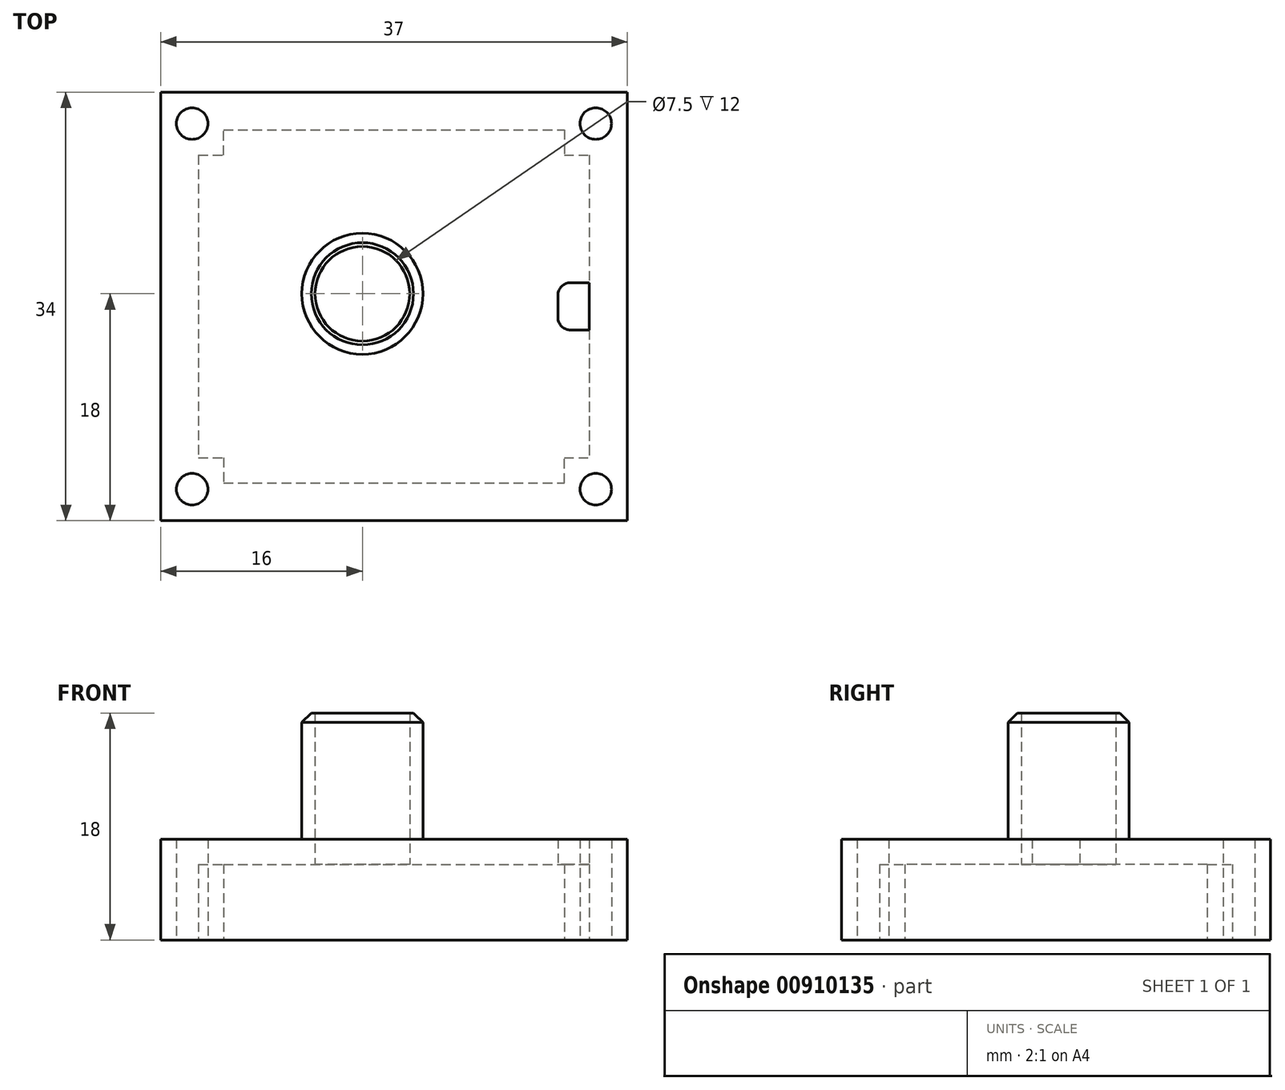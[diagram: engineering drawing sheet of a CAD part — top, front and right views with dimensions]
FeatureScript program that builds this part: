
annotation { "Feature Type Name" : "Feature", "Feature Type Description" : "" }
export const myFeature = defineFeature(function(context is Context, id is Id, definition is map)
    precondition{}
    {
        {
            var Q0;
            Q0=qCreatedBy(makeId("Top.planeOp"),FACE);
            var sketch = newSketch(context, id + "F0", { "sketchPlane" : qUnion([Q0])});
            skCircle(sketch, "E0", {"center": v(0, 0) * mm, "radius": 3.75 * mm});
            skCircle(sketch, "E1", {"center": v(0, 0) * mm, "radius": 4.8 * mm});
            skLineSegment(sketch, "E2.bottom", {"start": v(-13, 13) * mm, "end": v(18, 13) * mm});
            skLineSegment(sketch, "E2.top", {"start": v(-13, -15) * mm, "end": v(18, -15) * mm});
            skLineSegment(sketch, "E2.left", {"start": v(-13, 13) * mm, "end": v(-13, -15) * mm});
            skLineSegment(sketch, "E2.right", {"start": v(18, 13) * mm, "end": v(18, -15) * mm});
            skLineSegment(sketch, "E3.bottom", {"start": v(-16, 16) * mm, "end": v(21, 16) * mm});
            skLineSegment(sketch, "E3.top", {"start": v(-16, -18) * mm, "end": v(21, -18) * mm});
            skLineSegment(sketch, "E3.left", {"start": v(-16, 16) * mm, "end": v(-16, -18) * mm});
            skLineSegment(sketch, "E3.right", {"start": v(21, 16) * mm, "end": v(21, -18) * mm});
            skCircle(sketch, "E4", {"center": v(-13.5, 13.5) * mm, "radius": 1.25 * mm});
            skCircle(sketch, "E5", {"center": v(18.5, 13.5) * mm, "radius": 1.25 * mm});
            skCircle(sketch, "E6", {"center": v(18.5, -15.5) * mm, "radius": 1.25 * mm});
            skCircle(sketch, "E7", {"center": v(-13.5, -15.5) * mm, "radius": 1.25 * mm});
            skLineSegment(sketch, "E8.bottom", {"start": v(18, 0.88) * mm, "end": v(15.5, 0.88) * mm});
            skLineSegment(sketch, "E8.top", {"start": v(18, -2.87) * mm, "end": v(15.5, -2.87) * mm});
            skLineSegment(sketch, "E8.left", {"start": v(18, 0.88) * mm, "end": v(18, -2.87) * mm});
            skLineSegment(sketch, "E8.right", {"start": v(15.5, 0.88) * mm, "end": v(15.5, -2.87) * mm});
            skLineSegment(sketch, "E9", {"start": v(-13, -13) * mm, "end": v(-11, -13) * mm});
            skLineSegment(sketch, "E10", {"start": v(-11, -13) * mm, "end": v(-11, -15) * mm});
            skLineSegment(sketch, "E11", {"start": v(16, -15) * mm, "end": v(16, -13) * mm});
            skLineSegment(sketch, "E12", {"start": v(16, -13) * mm, "end": v(18, -13) * mm});
            skLineSegment(sketch, "E13", {"start": v(-13, 11) * mm, "end": v(-11, 11) * mm});
            skLineSegment(sketch, "E14", {"start": v(-11, 11) * mm, "end": v(-11, 13) * mm});
            skLineSegment(sketch, "E15", {"start": v(16, 13) * mm, "end": v(16, 11) * mm});
            skLineSegment(sketch, "E16", {"start": v(16, 11) * mm, "end": v(18, 11) * mm});
            skSolve(sketch);
        }
        {
            var Q0;
            {var subQ3=sQuery(id+"F0.wireOp",EDGE,"E2.bottom");Q0=makeQuery(id+"F0.imprint","IMPRINT",FACE,{"disambiguationData":[TD([[makeQuery(id+"F0.imprint","IMPRINT",EDGE,{"derivedFrom":subQ3}),1.0]])]});}
            var Q1;
            {var subQ4=sQuery(id+"F0.wireOp",EDGE,"E9");Q1=makeQuery(id+"F0.imprint","IMPRINT",FACE,{"disambiguationData":[TD([[makeQuery(id+"F0.imprint","IMPRINT",EDGE,{"derivedFrom":subQ4}),-1.0]])]});}
            var Q2;
            {var subQ3=sQuery(id+"F0.wireOp",EDGE,"E11");Q2=makeQuery(id+"F0.imprint","IMPRINT",FACE,{"disambiguationData":[TD([[makeQuery(id+"F0.imprint","IMPRINT",EDGE,{"derivedFrom":subQ3}),-1.0]])]});}
            var Q3;
            {var subQ3=sQuery(id+"F0.wireOp",EDGE,"E15");Q3=makeQuery(id+"F0.imprint","IMPRINT",FACE,{"disambiguationData":[TD([[makeQuery(id+"F0.imprint","IMPRINT",EDGE,{"derivedFrom":subQ3}),1.0]])]});}
            var Q4;
            {var subQ4=sQuery(id+"F0.wireOp",EDGE,"E13");Q4=makeQuery(id+"F0.imprint","IMPRINT",FACE,{"disambiguationData":[TD([[makeQuery(id+"F0.imprint","IMPRINT",EDGE,{"derivedFrom":subQ4}),1.0]])]});}
            extrude(context, id + "F1", {"entities" : qUnion([Q0, Q1, Q2, Q3, Q4]), "depth" : 8 * mm, "offsetDistance" : 25 * mm});
        }
        {
            var Q0;
            Q0=makeQuery(id+"F0.imprint","IMPRINT",FACE,{"disambiguationData":[TD([[makeQuery(id+"F0.imprint","IMPRINT",EDGE,{"derivedFrom":sQuery(id+"F0.wireOp",EDGE,"E1")}),-1.0]])]});
            extrude(context, id + "F2", {"entities" : qUnion([Q0]), "operationType" : NewBodyOperationType.ADD, "depth" : 8 * mm, "offsetDistance" : 25 * mm, "hasSecondDirection" : true, "secondDirectionOppositeDirection" : false, "secondDirectionDepth" : 6 * mm});
        }
        {
            var Q0;
            Q0=makeQuery(id+"F2.opExtrude","SWEPT_EDGE",EDGE,{"disambiguationData":[OSD([sQuery(id+"F0.wireOp",EDGE,"E8.bottom"),sQuery(id+"F0.wireOp",EDGE,"E8.right")])]});
            var Q1;
            Q1=makeQuery(id+"F2.opExtrude","SWEPT_EDGE",EDGE,{"disambiguationData":[OSD([sQuery(id+"F0.wireOp",EDGE,"E2.right"),sQuery(id+"F0.wireOp",EDGE,"E8.bottom"),sQuery(id+"F0.wireOp",EDGE,"E8.left")])]});
            var Q2;
            Q2=makeQuery(id+"F2.opExtrude","SWEPT_EDGE",EDGE,{"disambiguationData":[OSD([sQuery(id+"F0.wireOp",EDGE,"E8.top"),sQuery(id+"F0.wireOp",EDGE,"E8.right")])]});
            var Q3;
            Q3=makeQuery(id+"F2.opExtrude","SWEPT_EDGE",EDGE,{"disambiguationData":[OSD([sQuery(id+"F0.wireOp",EDGE,"E2.right"),sQuery(id+"F0.wireOp",EDGE,"E8.top"),sQuery(id+"F0.wireOp",EDGE,"E8.left")])]});
            fillet(context, id + "F3", {"entities" : qUnion([Q0, Q1, Q2, Q3]), "radius" : 1 * mm, "tangentPropagation" : true, "allowEdgeOverflow" : false});
        }
        {
            var Q0;
            Q0=makeQuery(id+"F0.imprint","IMPRINT",FACE,{"disambiguationData":[TD([[makeQuery(id+"F0.imprint","IMPRINT",EDGE,{"derivedFrom":sQuery(id+"F0.wireOp",EDGE,"E0")}),-1.0]])]});
            extrude(context, id + "F4", {"entities" : qUnion([Q0]), "operationType" : NewBodyOperationType.ADD, "depth" : 18 * mm, "offsetDistance" : 25 * mm, "hasSecondDirection" : true, "secondDirectionOppositeDirection" : false, "secondDirectionDepth" : 6 * mm});
        }
        {
            var Q0;
            Q0=makeQuery(id+"F4.opExtrude","CAP_EDGE",EDGE,{"disambiguationData":[OSD([sQuery(id+"F0.wireOp",EDGE,"E1")])],"isStart":false});
            chamfer(context, id + "F5", {"entities" : qUnion([Q0]), "width" : 0.75 * mm, "tangentPropagation" : true});
        }
    });
